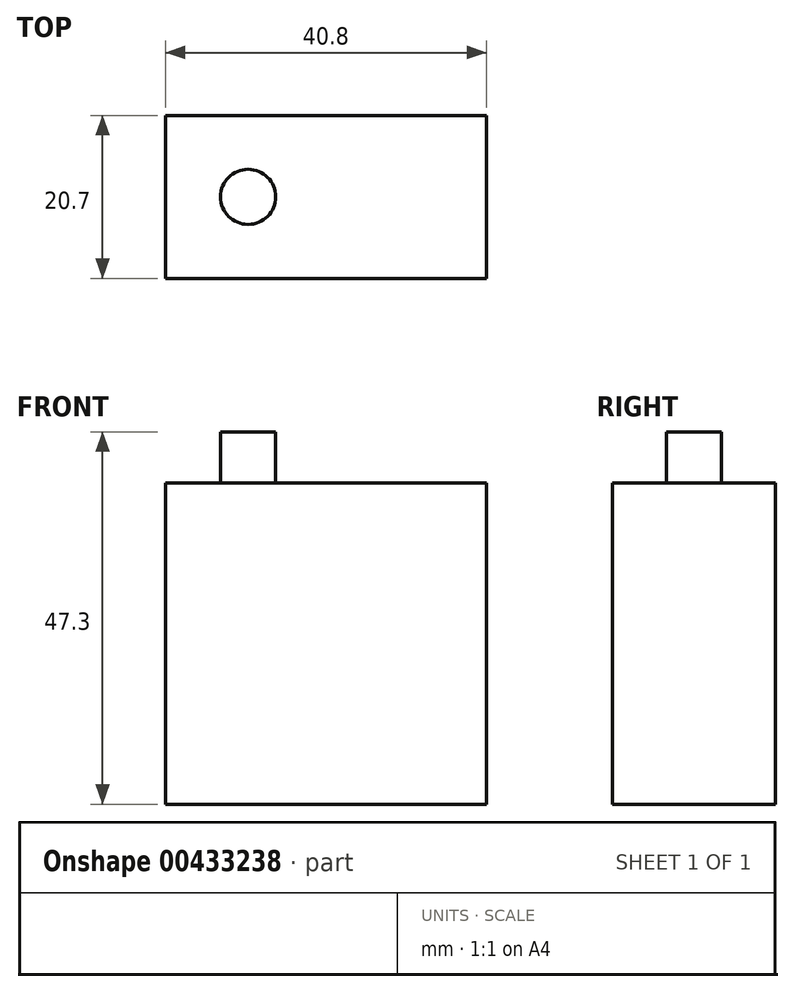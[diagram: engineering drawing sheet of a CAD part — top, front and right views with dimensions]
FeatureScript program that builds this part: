
annotation { "Feature Type Name" : "Feature", "Feature Type Description" : "" }
export const myFeature = defineFeature(function(context is Context, id is Id, definition is map)
    precondition{}
    {
        {
            var Q0;
            Q0=qCreatedBy(makeId("Top.planeOp"),FACE);
            var sketch = newSketch(context, id + "F0", { "sketchPlane" : qUnion([Q0])});
            skLineSegment(sketch, "E0.bottom", {"start": v(-20.4, 10.35) * mm, "end": v(20.4, 10.35) * mm});
            skLineSegment(sketch, "E0.top", {"start": v(-20.4, -10.35) * mm, "end": v(20.4, -10.35) * mm});
            skLineSegment(sketch, "E0.left", {"start": v(-20.4, 10.35) * mm, "end": v(-20.4, -10.35) * mm});
            skLineSegment(sketch, "E0.right", {"start": v(20.4, 10.35) * mm, "end": v(20.4, -10.35) * mm});
            skPoint(sketch, "E0.middle", {"position": v(0, 0) * mm});
            skSolve(sketch);
        }
        {
            var Q0;
            Q0 = qSketchRegion(id + "F0", true);
            extrude(context, id + "F1", {"entities" : qUnion([Q0]), "depth" : 40.8 * mm});
        }
        {
            var Q0;
            Q0=makeQuery(id+"F1.opExtrude","CAP_FACE",FACE,{"disambiguationData":[OSD([sQuery(id+"F0.wireOp",EDGE,"E0.bottom"),sQuery(id+"F0.wireOp",EDGE,"E0.top"),sQuery(id+"F0.wireOp",EDGE,"E0.left"),sQuery(id+"F0.wireOp",EDGE,"E0.right")])],"isStart":false});
            var sketch = newSketch(context, id + "F2", { "sketchPlane" : qUnion([Q0])});
            skLineSegment(sketch, "E1", {"start": v(-20.4, 0) * mm, "end": v(-13.4, 0) * mm, "construction": true});
            skLineSegment(sketch, "E2", {"start": v(-13.4, 0) * mm, "end": v(-9.9, 0) * mm, "construction": true});
            skCircle(sketch, "E3", {"center": v(-9.9, 0) * mm, "radius": 3.5 * mm});
            skSolve(sketch);
        }
        {
            var Q0;
            Q0 = qSketchRegion(id + "F2", true);
            extrude(context, id + "F3", {"entities" : qUnion([Q0]), "operationType" : NewBodyOperationType.ADD, "depth" : 6.5 * mm});
        }
    });
